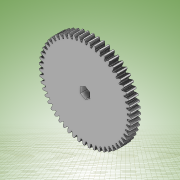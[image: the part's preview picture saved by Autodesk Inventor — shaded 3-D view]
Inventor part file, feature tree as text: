
AUTODESK INVENTOR PART (.ipt)
format: ipt  version: 2022 (Build 260153000, 153)  size: 2,759,680 bytes
history: native  units: mm
features: extrude x1, sketch x1
ambient origin geometry x8: Origin, YZ Plane, XZ Plane, XY Plane, X Axis, Y Axis, Z Axis, Center Point
bodies: Body1 (feature_tree)
feature tree (2):
  extrude  "Extrusión2"  Depth=6.0mm TaperAngle=0.0deg
  sketch  "Boceto4"  dims[d3=6.0mm d4=6.0mm d5=0.0mm]
